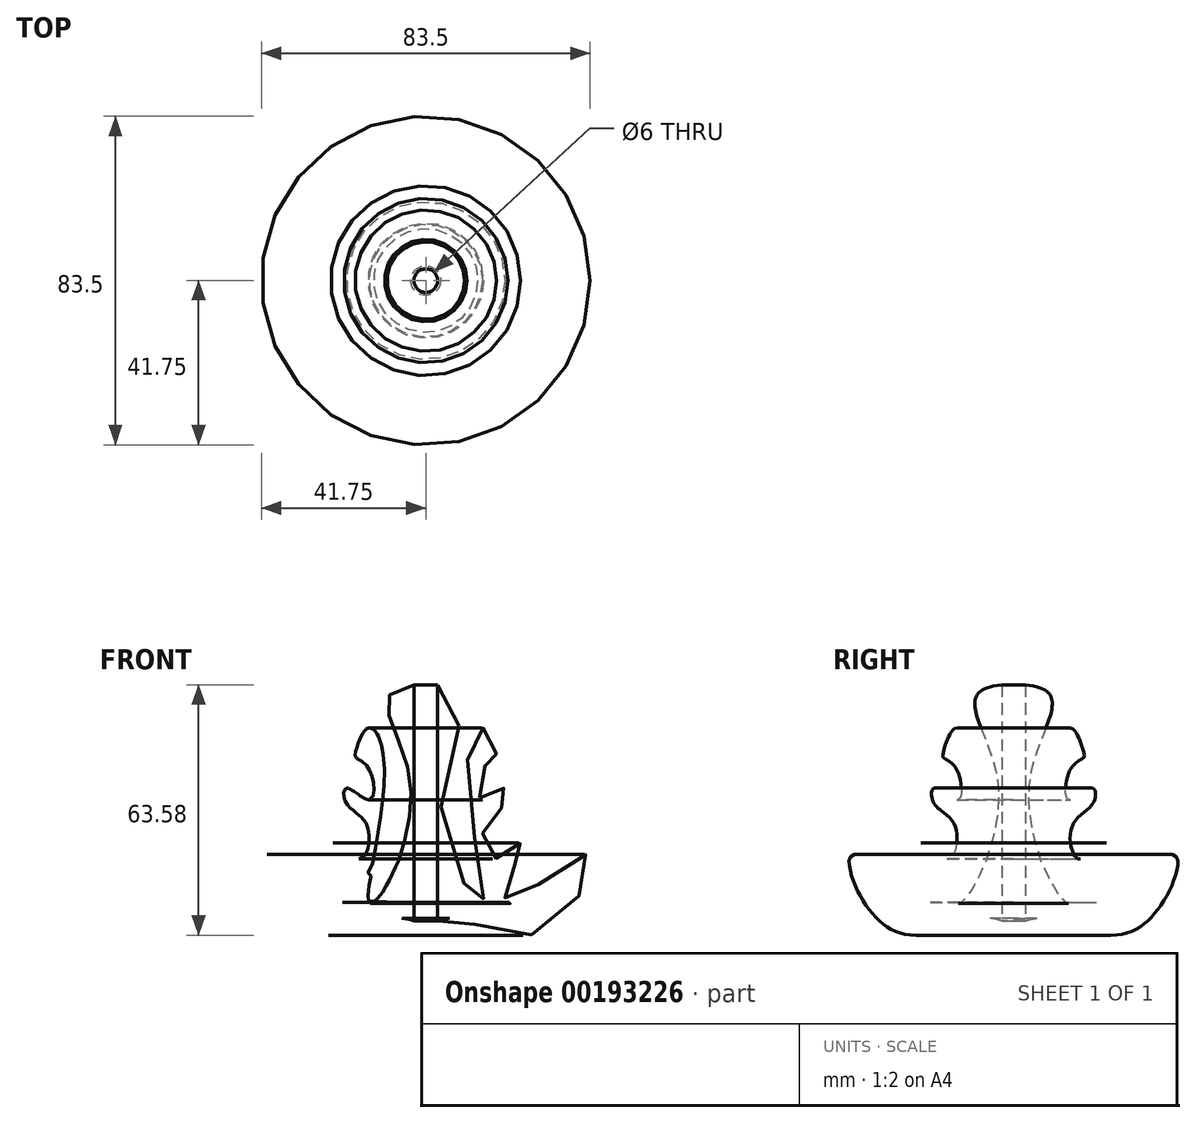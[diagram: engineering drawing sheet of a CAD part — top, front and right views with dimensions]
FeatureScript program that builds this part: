
annotation { "Feature Type Name" : "Feature", "Feature Type Description" : "" }
export const myFeature = defineFeature(function(context is Context, id is Id, definition is map)
    precondition{}
    {
        {
            var Q0;
            Q0=qCreatedBy(makeId("Right.planeOp"),FACE);
            var sketch = newSketch(context, id + "F0", { "sketchPlane" : qUnion([Q0])});
            skFitSpline(sketch, "E0", {"points": [v(0, 0) * mm, v(-7.39, 2.45) * mm, v(-31.48, 0) * mm, v(-40.7, 18.75) * mm, v(-20.95, 6.7) * mm, v(-21.78, 14.67) * mm, v(-23.92, 19.14) * mm, v(-23.57, 21.8) * mm, v(-16.81, 17.66) * mm, v(-14.9, 26.18) * mm, v(-20.22, 31.88) * mm, v(-20.11, 35.68) * mm, v(-14.2, 32.7) * mm, v(-14.42, 40.43) * mm, v(-17.66, 43.3) * mm, v(-17.95, 44.18) * mm, v(-14.88, 50.84) * mm, v(-10.49, 40.4) * mm, v(-14.15, 6.38) * mm, v(-4.24, 38.91) * mm, v(0, 61.97) * mm], "startDerivative": vector(-165.48, 121.63) * mm, "endDerivative": vector(720.52, -6.88) * mm});
            skLineSegment(sketch, "E1", {"start": v(0, 61.97) * mm, "end": v(0, 0) * mm});
            skSolve(sketch);
        }
        {
            var Q0;
            Q0=makeQuery(id+"F0.imprint","IMPRINT",FACE,{"disambiguationData":[TD([[makeQuery(id+"F0.imprint","IMPRINT",EDGE,{"derivedFrom":sQuery(id+"F0.wireOp",EDGE,"E0")}),-1.0]])]});
            var Q1;
            Q1=sQuery(id+"F0.wireOp",EDGE,"E1");
            revolve(context, id + "F1", {"entities" : qUnion([Q0]), "axis" : qUnion([Q1]), "revolveType" : RevolveType.FULL});
        }
        {
            var Q0;
            Q0=qCreatedBy(makeId("Top.planeOp"),FACE);
            var sketch = newSketch(context, id + "F2", { "sketchPlane" : qUnion([Q0])});
            skCircle(sketch, "E2", {"center": v(0, 0) * mm, "radius": 3 * mm});
            skSolve(sketch);
        }
        {
            var Q0;
            Q0 = qSketchRegion(id + "F2", true);
            var Q1;
            Q1=makeQuery(id+"F1.opRevolve","SWEPT_FACE",FACE,{"disambiguationData":[OSD([sQuery(id+"F0.wireOp",EDGE,"E0")])]});
            extrude(context, id + "F3", {"entities" : qUnion([Q0]), "operationType" : NewBodyOperationType.REMOVE, "endBoundEntityFace" : qUnion([Q1]), "depth" : 65.53 * mm});
        }
    });
